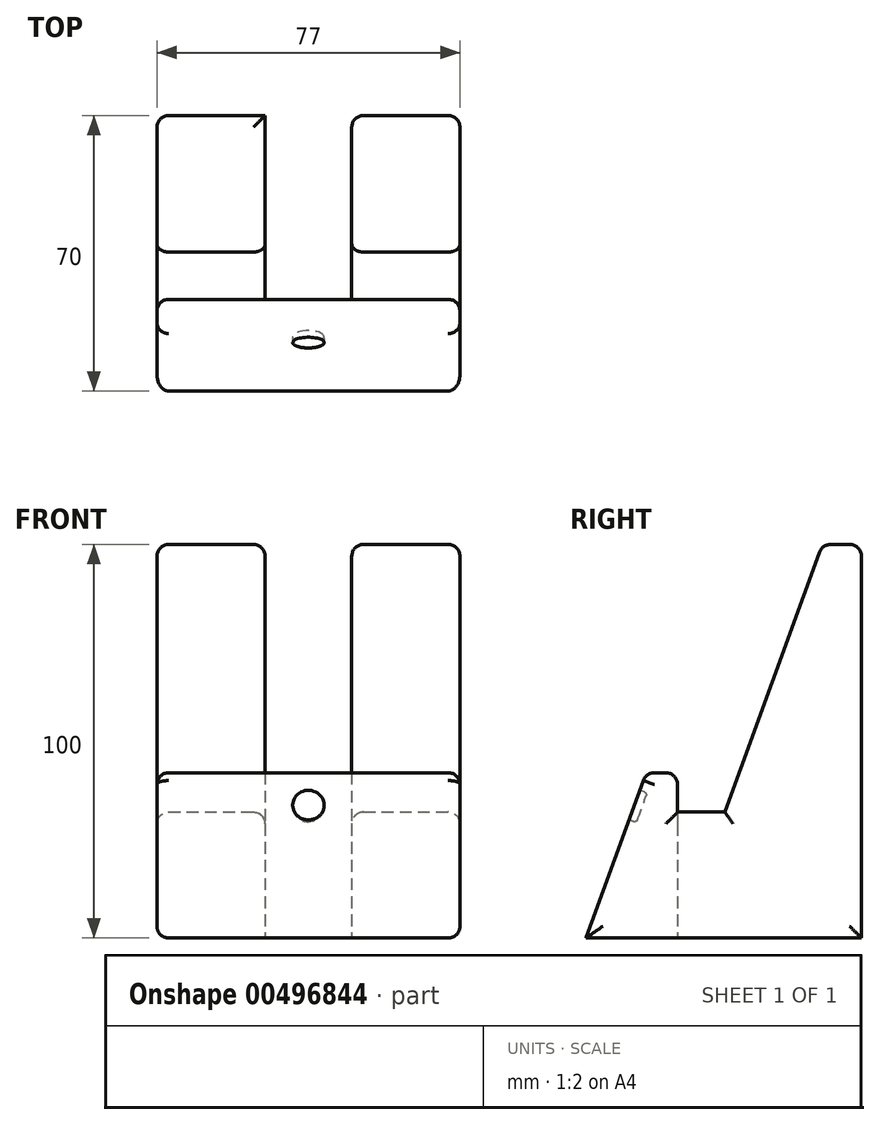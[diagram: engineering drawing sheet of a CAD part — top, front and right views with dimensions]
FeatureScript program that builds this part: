
annotation { "Feature Type Name" : "Feature", "Feature Type Description" : "" }
export const myFeature = defineFeature(function(context is Context, id is Id, definition is map)
    precondition{}
    {
        {
            var Q0;
            Q0=qCreatedBy(makeId("Right.planeOp"),FACE);
            var sketch = newSketch(context, id + "F0", { "sketchPlane" : qUnion([Q0])});
            skLineSegment(sketch, "E0", {"start": v(0, 0) * mm, "end": v(-70, 0) * mm});
            skLineSegment(sketch, "E1", {"start": v(-70, 0) * mm, "end": v(-54.71, 42) * mm});
            skLineSegment(sketch, "E2", {"start": v(-54.71, 42) * mm, "end": v(-46.71, 42) * mm});
            skLineSegment(sketch, "E3", {"start": v(-46.71, 42) * mm, "end": v(-46.71, 32) * mm});
            skLineSegment(sketch, "E4", {"start": v(-46.71, 32) * mm, "end": v(-34.71, 32) * mm});
            skLineSegment(sketch, "E5", {"start": v(-34.71, 32) * mm, "end": v(-9.96, 100) * mm});
            skLineSegment(sketch, "E6", {"start": v(-9.96, 100) * mm, "end": v(0, 100) * mm});
            skLineSegment(sketch, "E7", {"start": v(0, 100) * mm, "end": v(0, 0) * mm});
            skSolve(sketch);
        }
        {
            var Q0;
            Q0=makeQuery(id+"F0.imprint","IMPRINT",FACE,{"disambiguationData":[TD([[makeQuery(id+"F0.imprint","IMPRINT",EDGE,{"derivedFrom":sQuery(id+"F0.wireOp",EDGE,"E0")}),-1.0]])]});
            extrude(context, id + "F1", {"entities" : qUnion([Q0]), "endBound" : BoundingType.SYMMETRIC, "oppositeDirection" : true, "depth" : 77 * mm});
        }
        {
            var Q0;
            Q0=makeQuery(id+"F1.opExtrude","SWEPT_FACE",FACE,{"disambiguationData":[OSD([sQuery(id+"F0.wireOp",EDGE,"E7")])]});
            var sketch = newSketch(context, id + "F2", { "sketchPlane" : qUnion([Q0])});
            skLineSegment(sketch, "E8.bottom", {"start": v(-11, 100) * mm, "end": v(11, 100) * mm});
            skLineSegment(sketch, "E8.top", {"start": v(-11, 0) * mm, "end": v(11, 0) * mm});
            skLineSegment(sketch, "E8.left", {"start": v(-11, 100) * mm, "end": v(-11, 0) * mm});
            skLineSegment(sketch, "E8.right", {"start": v(11, 100) * mm, "end": v(11, 0) * mm});
            skPoint(sketch, "E8.middle", {"position": v(0, 50) * mm});
            skSolve(sketch);
        }
        {
            var Q0;
            Q0=qSketchRegion(id+"F2",true);
            var Q1;
            Q1=makeQuery(id+"F1.opExtrude","SWEPT_FACE",FACE,{"disambiguationData":[OSD([sQuery(id+"F0.wireOp",EDGE,"E3")])]});
            extrude(context, id + "F3", {"entities" : qUnion([Q0]), "operationType" : NewBodyOperationType.REMOVE, "endBound" : BoundingType.UP_TO_SURFACE, "oppositeDirection" : true, "endBoundEntityFace" : qUnion([Q1]), "depth" : 46.7 * mm});
        }
        {
            var Q0;
            Q0=makeQuery(id+"F1.opExtrude","SWEPT_FACE",FACE,{"disambiguationData":[OSD([sQuery(id+"F0.wireOp",EDGE,"E1")])]});
            var sketch = newSketch(context, id + "F4", { "sketchPlane" : qUnion([Q0])});
            skCircle(sketch, "E9", {"center": v(0, 12) * mm, "radius": 4 * mm});
            skPoint(sketch, "E10", {"position": v(0, 0) * mm});
            skSolve(sketch);
        }
        {
            var Q0;
            Q0=makeQuery(id+"F4.imprint","IMPRINT",FACE,{"disambiguationData":[TD([[makeQuery(id+"F4.imprint","IMPRINT",EDGE,{"derivedFrom":sQuery(id+"F4.wireOp",EDGE,"E9")}),1.0]])]});
            extrude(context, id + "F5", {"entities" : qUnion([Q0]), "operationType" : NewBodyOperationType.REMOVE, "oppositeDirection" : true, "depth" : 2 * mm});
        }
        {
            var Q0;
            Q0=makeQuery(id+"F5.boolean.opBoolean","COPY",EDGE,{"derivedFrom":makeQuery(id+"F5.opExtrude","CAP_EDGE",EDGE,{"disambiguationData":[OSD([sQuery(id+"F4.wireOp",EDGE,"E9")])],"isStart":false})});
            var Q1;
            Q1=makeQuery(id+"F5.boolean.opBoolean","COPY",EDGE,{"derivedFrom":makeQuery(id+"F5.opExtrude","CAP_EDGE",EDGE,{"disambiguationData":[OSD([sQuery(id+"F4.wireOp",EDGE,"E9")])],"isStart":true})});
            fillet(context, id + "F6", {"entities" : qUnion([Q0, Q1]), "radius" : .75 * mm, "tangentPropagation" : true, "allowEdgeOverflow" : false});
        }
        {
            var Q0;
            Q0=makeQuery(id+"F1.opExtrude","CAP_FACE",FACE,{"disambiguationData":[OSD([sQuery(id+"F0.wireOp",EDGE,"E0"),sQuery(id+"F0.wireOp",EDGE,"E1"),sQuery(id+"F0.wireOp",EDGE,"E2"),sQuery(id+"F0.wireOp",EDGE,"E3"),sQuery(id+"F0.wireOp",EDGE,"E4"),sQuery(id+"F0.wireOp",EDGE,"E5"),sQuery(id+"F0.wireOp",EDGE,"E6"),sQuery(id+"F0.wireOp",EDGE,"E7")])],"isStart":true});
            var Q1;
            Q1=makeQuery(id+"F1.opExtrude","CAP_FACE",FACE,{"disambiguationData":[OSD([sQuery(id+"F0.wireOp",EDGE,"E0"),sQuery(id+"F0.wireOp",EDGE,"E1"),sQuery(id+"F0.wireOp",EDGE,"E2"),sQuery(id+"F0.wireOp",EDGE,"E3"),sQuery(id+"F0.wireOp",EDGE,"E4"),sQuery(id+"F0.wireOp",EDGE,"E5"),sQuery(id+"F0.wireOp",EDGE,"E6"),sQuery(id+"F0.wireOp",EDGE,"E7")])],"isStart":false});
            var Q2;
            Q2=makeQuery(id+"F3.boolean.opBoolean","COPY",EDGE,{"derivedFrom":makeQuery(id+"F3.opExtrude","CAP_EDGE",EDGE,{"disambiguationData":[OSD([sQuery(id+"F2.wireOp",EDGE,"E8.right")])],"isStart":true})});
            var Q3;
            {var subQ1=sQuery(id+"F0.wireOp",EDGE,"E6");Q3=makeQuery(id+"F3.boolean.opBoolean","SPLIT",FACE,{"disambiguationData":[TD([makeQuery(id+"F3.opExtrude","SWEPT_FACE",FACE,{"disambiguationData":[OSD([sQuery(id+"F2.wireOp",EDGE,"E8.right")])]})])],"derivedFrom":makeQuery(id+"F1.opExtrude","SWEPT_FACE",FACE,{"disambiguationData":[OSD([subQ1])]})});}
            var Q4;
            {var subQ1=sQuery(id+"F0.wireOp",EDGE,"E6");Q4=makeQuery(id+"F3.boolean.opBoolean","SPLIT",FACE,{"disambiguationData":[TD([makeQuery(id+"F3.opExtrude","SWEPT_FACE",FACE,{"disambiguationData":[OSD([sQuery(id+"F2.wireOp",EDGE,"E8.left")])]})])],"derivedFrom":makeQuery(id+"F1.opExtrude","SWEPT_FACE",FACE,{"disambiguationData":[OSD([subQ1])]})});}
            var Q5;
            Q5=makeQuery(id+"F3.boolean.opBoolean","COPY",EDGE,{"derivedFrom":makeQuery(id+"F3.opExtrude","CAP_EDGE",EDGE,{"disambiguationData":[OSD([sQuery(id+"F2.wireOp",EDGE,"E8.left")])],"isStart":true})});
            var Q6;
            Q6=makeQuery(id+"F3.boolean.opBoolean","INTERSECT",EDGE,{"derivedFrom":[makeQuery(id+"F1.opExtrude","SWEPT_FACE",FACE,{"disambiguationData":[OSD([sQuery(id+"F0.wireOp",EDGE,"E5")])]}),makeQuery(id+"F3.opExtrude","SWEPT_FACE",FACE,{"disambiguationData":[OSD([sQuery(id+"F2.wireOp",EDGE,"E8.left")])]})]});
            var Q7;
            Q7=makeQuery(id+"F3.boolean.opBoolean","INTERSECT",EDGE,{"derivedFrom":[makeQuery(id+"F1.opExtrude","SWEPT_FACE",FACE,{"disambiguationData":[OSD([sQuery(id+"F0.wireOp",EDGE,"E5")])]}),makeQuery(id+"F3.opExtrude","SWEPT_FACE",FACE,{"disambiguationData":[OSD([sQuery(id+"F2.wireOp",EDGE,"E8.right")])]})]});
            fillet(context, id + "F7", {"entities" : qUnion([Q0, Q1, Q2, Q3, Q4, Q5, Q6, Q7]), "radius" : 3 * mm, "tangentPropagation" : true, "allowEdgeOverflow" : false});
        }
        {
            var Q0;
            Q0=makeQuery(id+"F1.opExtrude","SWEPT_EDGE",EDGE,{"disambiguationData":[OSD([sQuery(id+"F0.wireOp",EDGE,"E1"),sQuery(id+"F0.wireOp",EDGE,"E2")])]});
            var Q1;
            Q1=makeQuery(id+"F1.opExtrude","SWEPT_EDGE",EDGE,{"disambiguationData":[OSD([sQuery(id+"F0.wireOp",EDGE,"E2"),sQuery(id+"F0.wireOp",EDGE,"E3")])]});
            var Q2;
            Q2=makeQuery(id+"F3.boolean.opBoolean","INTERSECT",EDGE,{"derivedFrom":[makeQuery(id+"F1.opExtrude","SWEPT_FACE",FACE,{"disambiguationData":[OSD([sQuery(id+"F0.wireOp",EDGE,"E4")])]}),makeQuery(id+"F3.opExtrude","SWEPT_FACE",FACE,{"disambiguationData":[OSD([sQuery(id+"F2.wireOp",EDGE,"E8.right")])]})]});
            var Q3;
            Q3=makeQuery(id+"F3.boolean.opBoolean","INTERSECT",EDGE,{"derivedFrom":[makeQuery(id+"F1.opExtrude","SWEPT_FACE",FACE,{"disambiguationData":[OSD([sQuery(id+"F0.wireOp",EDGE,"E4")])]}),makeQuery(id+"F3.opExtrude","SWEPT_FACE",FACE,{"disambiguationData":[OSD([sQuery(id+"F2.wireOp",EDGE,"E8.left")])]})]});
            fillet(context, id + "F8", {"entities" : qUnion([Q0, Q1, Q2, Q3]), "radius" : 3 * mm, "tangentPropagation" : true, "allowEdgeOverflow" : false});
        }
    });
